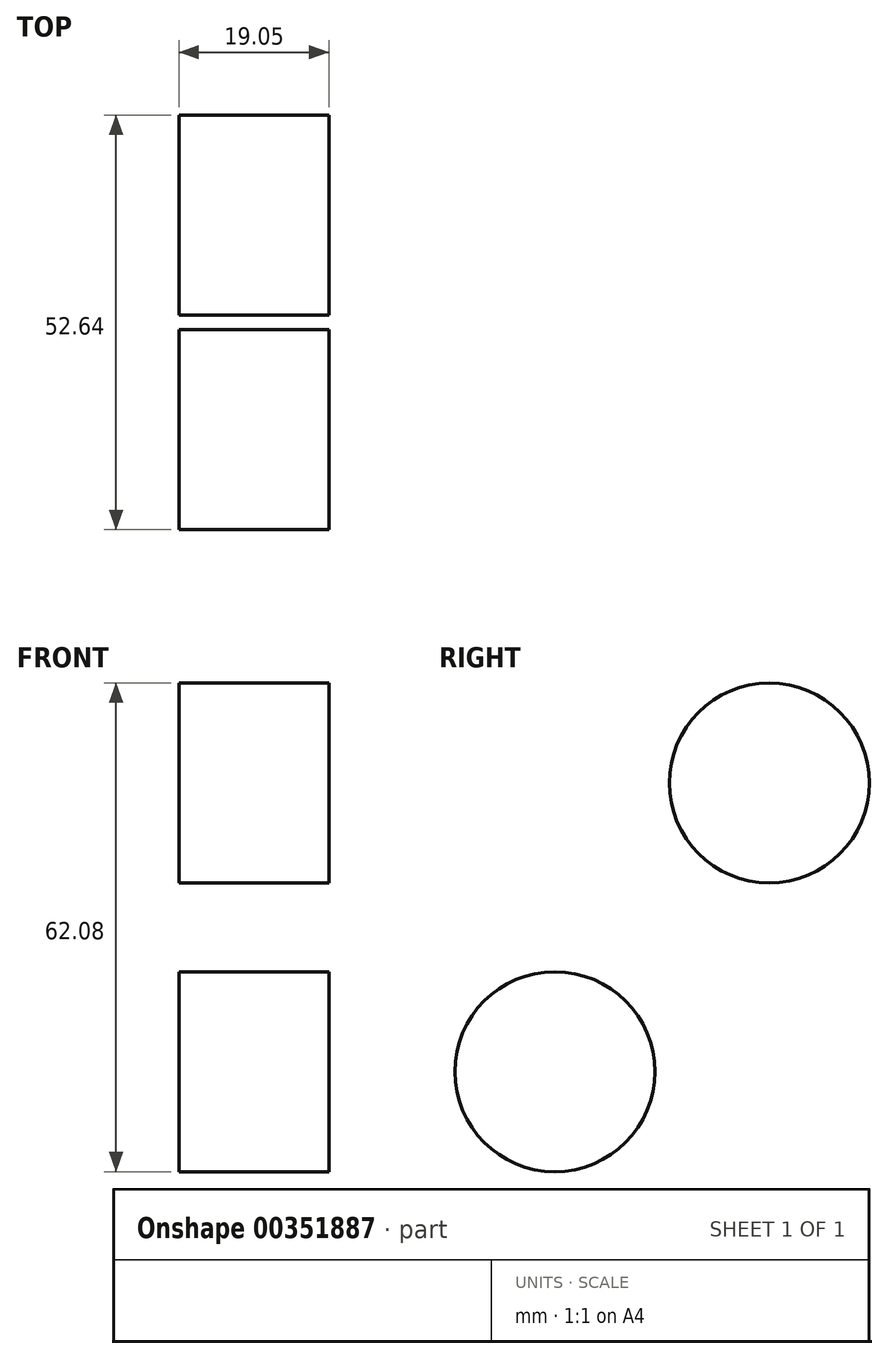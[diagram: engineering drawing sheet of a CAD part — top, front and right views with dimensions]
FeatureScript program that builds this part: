
annotation { "Feature Type Name" : "Feature", "Feature Type Description" : "" }
export const myFeature = defineFeature(function(context is Context, id is Id, definition is map)
    precondition{}
    {
        {
            var Q0;
            Q0=qCreatedBy(makeId("Right.planeOp"),FACE);
            var sketch = newSketch(context, id + "F0", { "sketchPlane" : qUnion([Q0])});
            skCircle(sketch, "E0", {"center": v(0, 0) * mm, "radius": 12.7 * mm});
            skCircle(sketch, "E1", {"center": v(27.24, 36.68) * mm, "radius": 12.7 * mm});
            skSolve(sketch);
        }
        {
            var Q0;
            Q0=makeQuery(id+"F0.imprint","IMPRINT",FACE,{"disambiguationData":[TD([[makeQuery(id+"F0.imprint","IMPRINT",EDGE,{"derivedFrom":sQuery(id+"F0.wireOp",EDGE,"E1")}),1.0]])]});
            var Q1;
            Q1=makeQuery(id+"F0.imprint","IMPRINT",FACE,{"disambiguationData":[TD([[makeQuery(id+"F0.imprint","IMPRINT",EDGE,{"derivedFrom":sQuery(id+"F0.wireOp",EDGE,"E0")}),1.0]])]});
            extrude(context, id + "F1", {"entities" : qUnion([Q0, Q1]), "depth" : 19.05 * mm});
        }
    });
